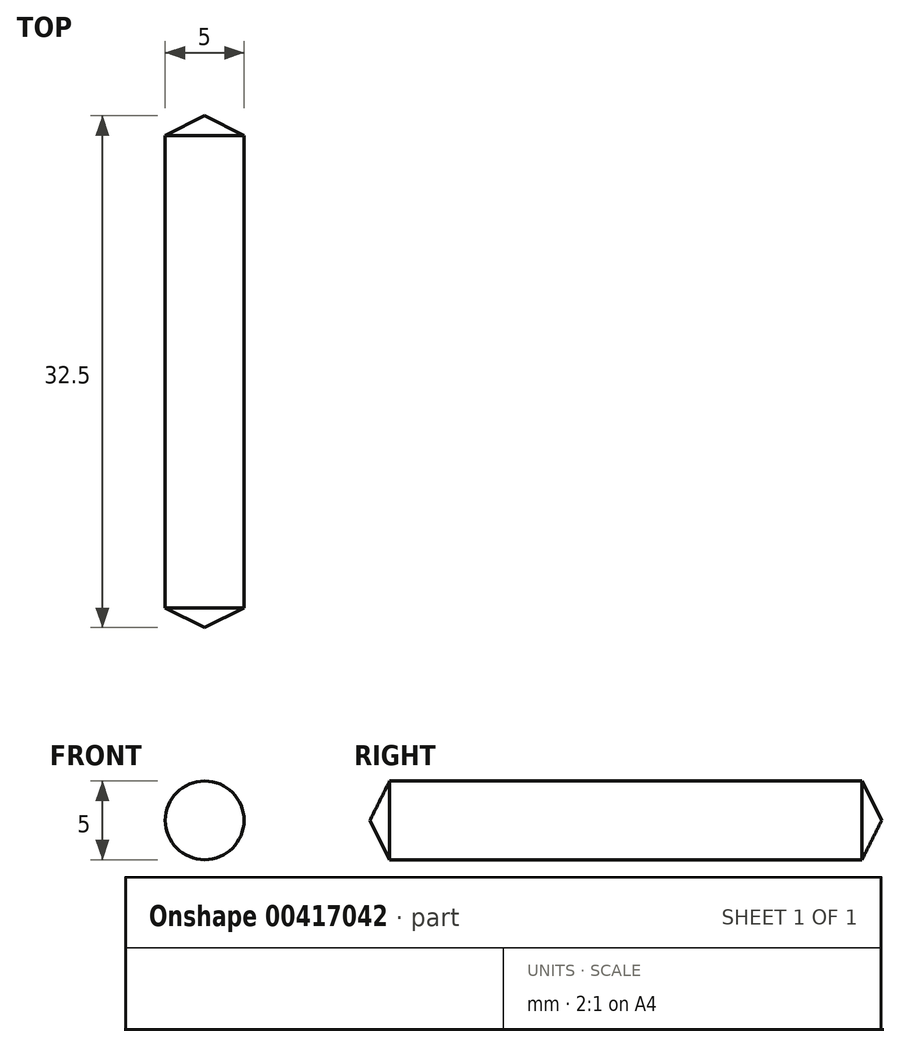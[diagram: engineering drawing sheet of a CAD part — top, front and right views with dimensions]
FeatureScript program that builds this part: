
annotation { "Feature Type Name" : "Feature", "Feature Type Description" : "" }
export const myFeature = defineFeature(function(context is Context, id is Id, definition is map)
    precondition{}
    {
        {
            var Q0;
            Q0=qCreatedBy(makeId("Front.planeOp"),FACE);
            var sketch = newSketch(context, id + "F0", { "sketchPlane" : qUnion([Q0])});
            skCircle(sketch, "E0", {"center": v(0, 0) * mm, "radius": 2.5 * mm});
            skSolve(sketch);
        }
        {
            var Q0;
            Q0 = qSketchRegion(id + "F0", true);
            extrude(context, id + "F1", {"entities" : qUnion([Q0]), "depth" : 30 * mm});
        }
        {
            var Q0;
            Q0=makeQuery(id+"F1.opExtrude","CAP_FACE",FACE,{"disambiguationData":[OSD([sQuery(id+"F0.wireOp",EDGE,"E0")])],"isStart":false});
            var sketch = newSketch(context, id + "F2", { "sketchPlane" : qUnion([Q0])});
            skPoint(sketch, "E1", {"position": v(0, 0) * mm});
            skLineSegment(sketch, "E2", {"start": v(0, 0) * mm, "end": v(0, 2.5) * mm});
            skSolve(sketch);
        }
        {
            var Q0;
            Q0=sQuery(id+"F2.wireOp",VERTEX,"E1");
            var Q1;
            Q1=qCreatedBy(makeId("Origin.pointOp"),VERTEX);
            var Q2;
            Q2=sQuery(id+"F2.wireOp",VERTEX,"E2.end");
            cPlane(context, id + "F3", {"entities" : qUnion([Q0, Q1, Q2]), "cplaneType" : CPlaneType.THREE_POINT, "offset" : 25 * mm, "width" : 150 * mm, "height" : 150 * mm});
        }
        {
            var Q0;
            Q0=qCreatedBy(id+"F3.planeOp",FACE);
            var sketch = newSketch(context, id + "F4", { "sketchPlane" : qUnion([Q0])});
            skLineSegment(sketch, "E3", {"start": v(29.94, 0) * mm, "end": v(0, 0) * mm, "construction": true});
            skSolve(sketch);
        }
        {
            var Q0;
            Q0=qCreatedBy(id+"F3.planeOp",FACE);
            var sketch = newSketch(context, id + "F5", { "sketchPlane" : qUnion([Q0])});
            skLineSegment(sketch, "E4", {"start": v(30, 0) * mm, "end": v(30, 2.5) * mm});
            skLineSegment(sketch, "E5", {"start": v(30, 2.5) * mm, "end": v(31.25, 0) * mm});
            skLineSegment(sketch, "E6", {"start": v(31.25, 0) * mm, "end": v(30, 0) * mm});
            skLineSegment(sketch, "E7", {"start": v(0, 0) * mm, "end": v(-1.25, 0) * mm});
            skLineSegment(sketch, "E8", {"start": v(-1.25, 0) * mm, "end": v(0, 2.5) * mm});
            skLineSegment(sketch, "E9", {"start": v(0, 2.5) * mm, "end": v(0, 0) * mm});
            skLineSegment(sketch, "E10", {"start": v(30, 2.5) * mm, "end": v(0, 2.5) * mm, "construction": true});
            skSolve(sketch);
        }
        {
            var Q0;
            Q0 = qSketchRegion(id + "F5", true);
            var Q1;
            Q1=sQuery(id+"F4.wireOp",EDGE,"E3");
            revolve(context, id + "F6", {"operationType" : NewBodyOperationType.ADD, "entities" : qUnion([Q0]), "axis" : qUnion([Q1]), "revolveType" : RevolveType.FULL});
        }
    });
